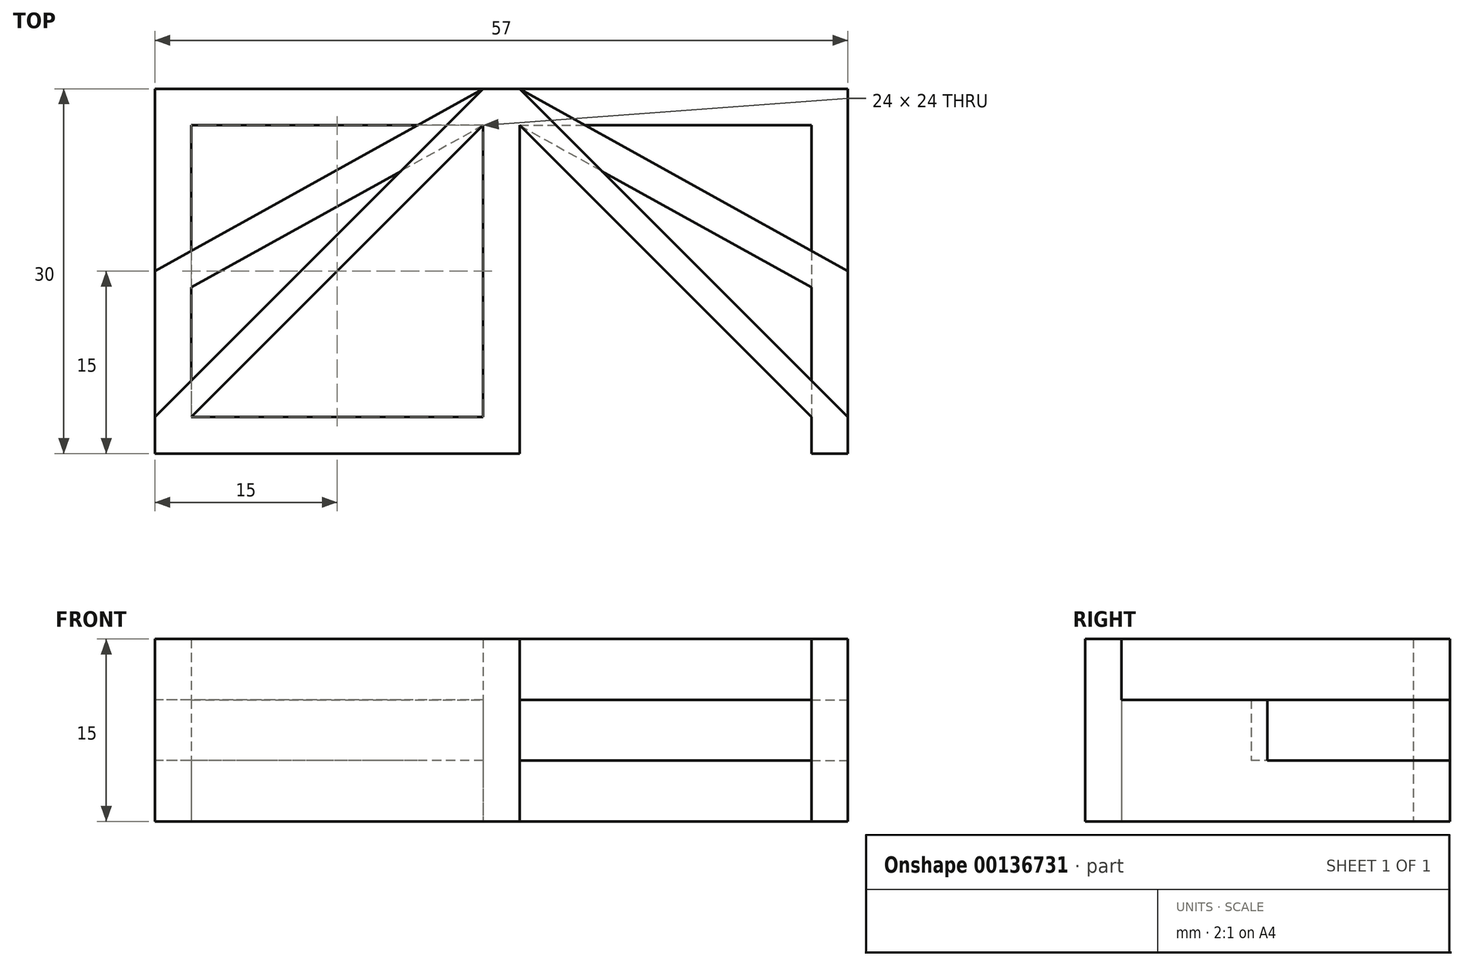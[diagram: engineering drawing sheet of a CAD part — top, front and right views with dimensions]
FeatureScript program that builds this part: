
annotation { "Feature Type Name" : "Feature", "Feature Type Description" : "" }
export const myFeature = defineFeature(function(context is Context, id is Id, definition is map)
    precondition{}
    {
        {
            var Q0;
            Q0=qCreatedBy(makeId("Top.planeOp"),FACE);
            var sketch = newSketch(context, id + "F0", { "sketchPlane" : qUnion([Q0])});
            skLineSegment(sketch, "E0", {"start": v(0, 0) * mm, "end": v(30, 0) * mm});
            skLineSegment(sketch, "E1", {"start": v(30, 0) * mm, "end": v(30, 30) * mm});
            skLineSegment(sketch, "E2", {"start": v(30, 30) * mm, "end": v(0, 30) * mm});
            skLineSegment(sketch, "E3", {"start": v(0, 30) * mm, "end": v(0, 0) * mm});
            skLineSegment(sketch, "E4.0", {"start": v(3, 27) * mm, "end": v(3, 3) * mm});
            skLineSegment(sketch, "E4.1", {"start": v(27, 27) * mm, "end": v(3, 27) * mm});
            skLineSegment(sketch, "E4.2", {"start": v(27, 3) * mm, "end": v(27, 27) * mm});
            skLineSegment(sketch, "E4.3", {"start": v(3, 3) * mm, "end": v(27, 3) * mm});
            skSolve(sketch);
        }
        {
            var Q0;
            Q0=makeQuery(id+"F0.imprint","IMPRINT",FACE,{"disambiguationData":[TD([[makeQuery(id+"F0.imprint","IMPRINT",EDGE,{"derivedFrom":sQuery(id+"F0.wireOp",EDGE,"E0")}),1.0]])]});
            extrude(context, id + "F1", {"entities" : qUnion([Q0]), "depth" : 5 * mm, "offsetDistance" : 25 * mm});
        }
        {
            var Q0;
            Q0=makeQuery(id+"F1.opExtrude","CAP_FACE",FACE,{"disambiguationData":[OSD([sQuery(id+"F0.wireOp",EDGE,"E0"),sQuery(id+"F0.wireOp",EDGE,"E1"),sQuery(id+"F0.wireOp",EDGE,"E2"),sQuery(id+"F0.wireOp",EDGE,"E3"),sQuery(id+"F0.wireOp",EDGE,"E4.0"),sQuery(id+"F0.wireOp",EDGE,"E4.1"),sQuery(id+"F0.wireOp",EDGE,"E4.2"),sQuery(id+"F0.wireOp",EDGE,"E4.3")])],"isStart":false});
            var sketch = newSketch(context, id + "F2", { "sketchPlane" : qUnion([Q0])});
            skLineSegment(sketch, "E5", {"start": v(0, 0) * mm, "end": v(30, 0) * mm});
            skLineSegment(sketch, "E6", {"start": v(30, 0) * mm, "end": v(30, 30) * mm});
            skLineSegment(sketch, "E7", {"start": v(30, 30) * mm, "end": v(27, 30) * mm});
            skLineSegment(sketch, "E8", {"start": v(27, 30) * mm, "end": v(0, 15) * mm});
            skLineSegment(sketch, "E9", {"start": v(0, 15) * mm, "end": v(0, 0) * mm});
            skLineSegment(sketch, "E10", {"start": v(27, 27) * mm, "end": v(3, 13.67) * mm});
            skSolve(sketch);
        }
        {
            var Q0;
            Q0=makeQuery(id+"F2.imprint","IMPRINT",FACE,{"disambiguationData":[TD([[makeQuery(id+"F2.imprint","IMPRINT",EDGE,{"derivedFrom":sQuery(id+"F2.wireOp",EDGE,"E5")}),1.0]])]});
            var Q1;
            {var subQ5=sQuery(id+"F2.wireOp",EDGE,"E10");Q1=makeQuery(id+"F2.imprint","IMPRINT",FACE,{"disambiguationData":[TD([[makeQuery(id+"F2.imprint","IMPRINT",EDGE,{"derivedFrom":subQ5}),-1.0]])]});}
            extrude(context, id + "F3", {"entities" : qUnion([Q0, Q1]), "operationType" : NewBodyOperationType.ADD, "depth" : 5 * mm, "offsetDistance" : 25 * mm});
        }
        {
            var Q0;
            Q0=makeQuery(id+"F3.opExtrude","CAP_FACE",FACE,{"disambiguationData":[OSD([sQuery(id+"F0.wireOp",EDGE,"E4.0"),sQuery(id+"F0.wireOp",EDGE,"E4.2"),sQuery(id+"F0.wireOp",EDGE,"E4.3"),sQuery(id+"F2.wireOp",EDGE,"E5"),sQuery(id+"F2.wireOp",EDGE,"E6"),sQuery(id+"F2.wireOp",EDGE,"E7"),sQuery(id+"F2.wireOp",EDGE,"E8"),sQuery(id+"F2.wireOp",EDGE,"E9"),sQuery(id+"F2.wireOp",EDGE,"E10")])],"isStart":false});
            var sketch = newSketch(context, id + "F4", { "sketchPlane" : qUnion([Q0])});
            skLineSegment(sketch, "E11", {"start": v(3, 3) * mm, "end": v(27, 27) * mm});
            skLineSegment(sketch, "E12", {"start": v(27, 30) * mm, "end": v(0, 3) * mm});
            skSolve(sketch);
        }
        {
            var Q0;
            {var subQ0=sQuery(id+"F4.wireOp",EDGE,"E11");Q0=makeQuery(id+"F4.imprint","IMPRINT",FACE,{"disambiguationData":[TD([[makeQuery(id+"F4.imprint","IMPRINT",EDGE,{"derivedFrom":subQ0}),1.0]])]});}
            var Q1;
            {var subQ0=makeQuery(id+"F3.opExtrude","CAP_EDGE",EDGE,{"disambiguationData":[OSD([sQuery(id+"F2.wireOp",EDGE,"E5")])],"isStart":false});Q1=makeQuery(id+"F4.imprint","IMPRINT",FACE,{"disambiguationData":[TD([[makeQuery(id+"F4.imprint","IMPRINT",EDGE,{"derivedFrom":subQ0}),1.0]])]});}
            extrude(context, id + "F5", {"entities" : qUnion([Q0, Q1]), "operationType" : NewBodyOperationType.ADD, "depth" : 5 * mm, "offsetDistance" : 25 * mm});
        }
        {
            var Q0;
            Q0=makeQuery(id+"F5.opExtrude","CAP_EDGE",EDGE,{"disambiguationData":[OSD([sQuery(id+"F2.wireOp",EDGE,"E7")])],"isStart":false});
            cPoint(context, id + "F6", {"entities" : qUnion([Q0]), "parameter" : 0.5});
        }
        {
            var Q0;
            Q0 = qCreatedBy(id + "F6" ,VERTEX);
            var Q1;
            Q1=makeQuery(id+"F5.opExtrude","CAP_EDGE",EDGE,{"disambiguationData":[OSD([sQuery(id+"F2.wireOp",EDGE,"E7")])],"isStart":false});
            cPlane(context, id + "F7", {"entities" : qUnion([Q0, Q1]), "cplaneType" : CPlaneType.LINE_POINT, "offset" : 25 * mm, "width" : 150 * mm, "height" : 150 * mm});
        }
        {
            var Q0;
            Q0=makeQuery(id+"F1.opExtrude","SWEPT_BODY",BODY,{"disambiguationData":[OSD([sQuery(id+"F0.wireOp",EDGE,"E0"),sQuery(id+"F0.wireOp",EDGE,"E1"),sQuery(id+"F0.wireOp",EDGE,"E2"),sQuery(id+"F0.wireOp",EDGE,"E3"),sQuery(id+"F0.wireOp",EDGE,"E4.0"),sQuery(id+"F0.wireOp",EDGE,"E4.1"),sQuery(id+"F0.wireOp",EDGE,"E4.2"),sQuery(id+"F0.wireOp",EDGE,"E4.3")])]});
            var Q1;
            Q1=qCreatedBy(id+"F7.planeOp",FACE);
            mirror(context, id + "F8", {"operationType" : NewBodyOperationType.ADD, "entities" : qUnion([Q0]), "mirrorPlane" : qUnion([Q1])});
        }
        {
            var Q0;
            {var subQ0=makeQuery(id+"F5.opExtrude","CAP_FACE",FACE,{"disambiguationData":[OSD([sQuery(id+"F0.wireOp",EDGE,"E4.2"),sQuery(id+"F0.wireOp",EDGE,"E4.3"),sQuery(id+"F2.wireOp",EDGE,"E5"),sQuery(id+"F2.wireOp",EDGE,"E6"),sQuery(id+"F2.wireOp",EDGE,"E7"),sQuery(id+"F2.wireOp",EDGE,"E9"),sQuery(id+"F4.wireOp",EDGE,"E11"),sQuery(id+"F4.wireOp",EDGE,"E12")])],"isStart":false});Q0=makeQuery(id+"F8.boolean.opBoolean","MERGE",FACE,{"derivedFrom":[subQ0,makeQuery(id+"F8.opPattern","COPY",FACE,{"derivedFrom":subQ0,"instanceName":"1"})]});}
            var sketch = newSketch(context, id + "F9", { "sketchPlane" : qUnion([Q0])});
            skLineSegment(sketch, "E13", {"start": v(30, 3) * mm, "end": v(30, 0) * mm});
            skLineSegment(sketch, "E14", {"start": v(30, 0) * mm, "end": v(54, 0) * mm});
            skLineSegment(sketch, "E15", {"start": v(54, 0) * mm, "end": v(54, 3) * mm});
            skLineSegment(sketch, "E16", {"start": v(54, 3) * mm, "end": v(30, 3) * mm});
            skSolve(sketch);
        }
        {
            var Q0;
            Q0=makeQuery(id+"F9.imprint","IMPRINT",FACE,{"disambiguationData":[TD([[makeQuery(id+"F9.imprint","IMPRINT",EDGE,{"derivedFrom":sQuery(id+"F9.wireOp",EDGE,"E13")}),1.0]])]});
            extrude(context, id + "F10", {"entities" : qUnion([Q0]), "operationType" : NewBodyOperationType.REMOVE, "oppositeDirection" : true, "depth" : 25 * mm, "offsetDistance" : 25 * mm});
        }
    });
